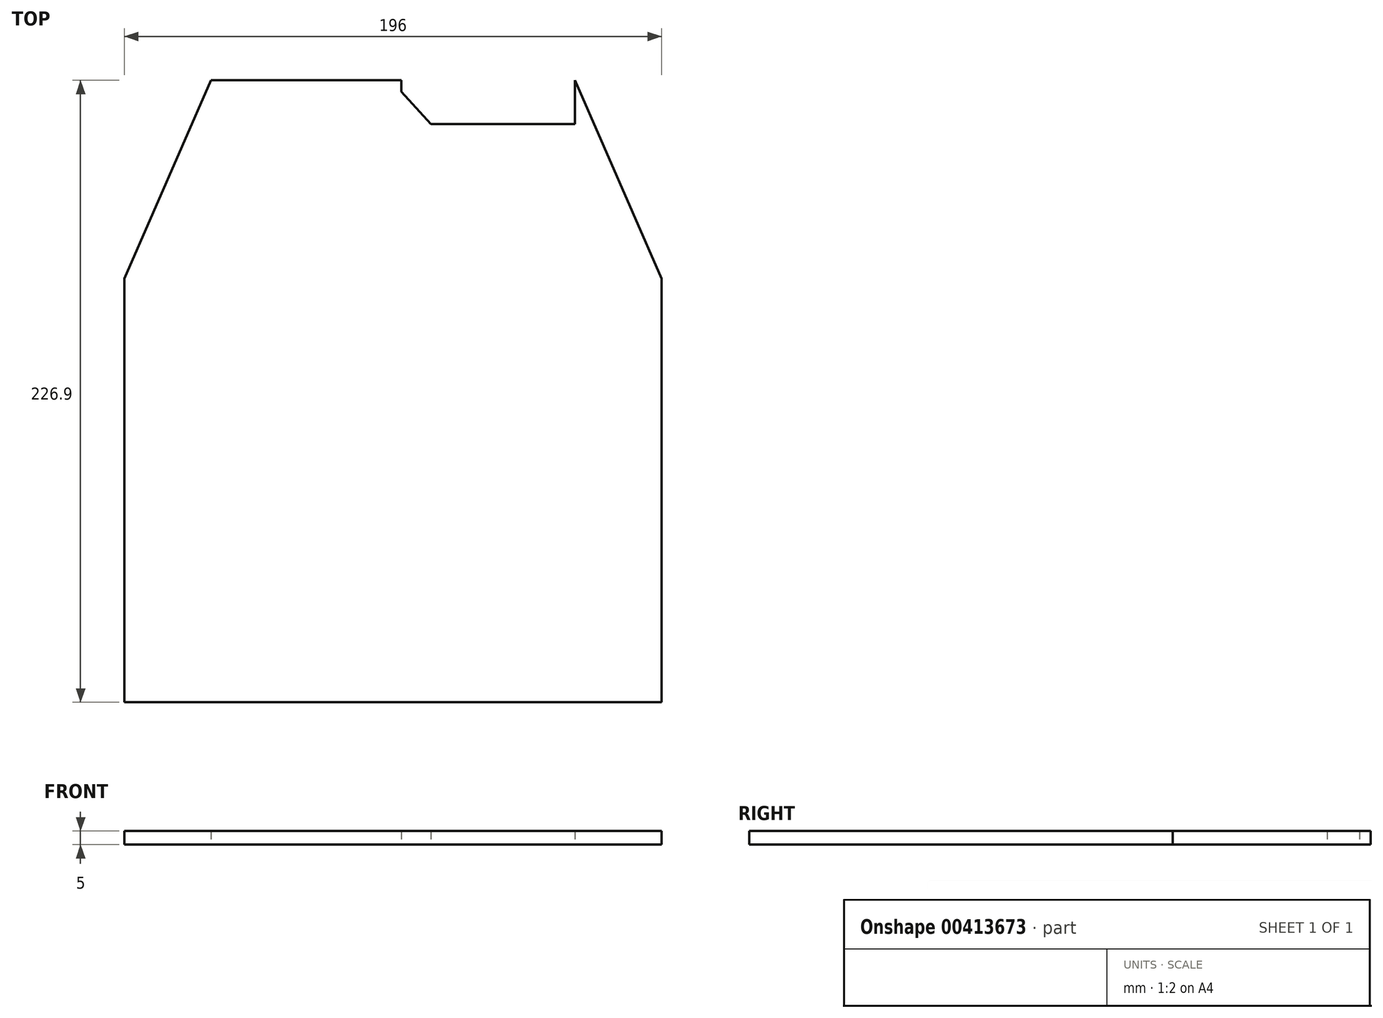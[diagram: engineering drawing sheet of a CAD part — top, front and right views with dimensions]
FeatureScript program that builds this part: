
annotation { "Feature Type Name" : "Feature", "Feature Type Description" : "" }
export const myFeature = defineFeature(function(context is Context, id is Id, definition is map)
    precondition{}
    {
        {
            var Q0;
            Q0=qCreatedBy(makeId("Top.planeOp"),FACE);
            var sketch = newSketch(context, id + "F0", { "sketchPlane" : qUnion([Q0])});
            skLineSegment(sketch, "E0", {"start": v(-98, 0) * mm, "end": v(98, 0) * mm});
            skLineSegment(sketch, "E1.0", {"start": v(13.9, 211) * mm, "end": v(66.4, 211) * mm});
            skLineSegment(sketch, "E2.0", {"start": v(-66.4, 226.9) * mm, "end": v(3.1, 226.9) * mm});
            skLineSegment(sketch, "E3", {"start": v(98, 0) * mm, "end": v(98, 154.6) * mm});
            skLineSegment(sketch, "E4", {"start": v(66.4, 226.9) * mm, "end": v(66.4, 211) * mm});
            skLineSegment(sketch, "E5", {"start": v(66.4, 226.9) * mm, "end": v(98, 154.6) * mm});
            skPoint(sketch, "E6.orphan", {"position": v(98, 226.9) * mm});
            skLineSegment(sketch, "E7", {"start": v(-66.4, 226.9) * mm, "end": v(-98, 154.6) * mm});
            skPoint(sketch, "E8.orphan", {"position": v(-98, 226.9) * mm});
            skLineSegment(sketch, "E9", {"start": v(-98, 0) * mm, "end": v(-98, 154.6) * mm});
            skLineSegment(sketch, "E10", {"start": v(3.1, 226.9) * mm, "end": v(3.1, 222.8) * mm});
            skLineSegment(sketch, "E11", {"start": v(3.1, 222.8) * mm, "end": v(13.9, 211) * mm});
            skSolve(sketch);
        }
        {
            var Q0;
            Q0 = qSketchRegion(id + "F0", true);
            extrude(context, id + "F1", {"entities" : qUnion([Q0]), "depth" : 5 * mm});
        }
    });
